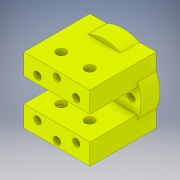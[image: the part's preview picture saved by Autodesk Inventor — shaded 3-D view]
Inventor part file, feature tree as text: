
AUTODESK INVENTOR PART (.ipt)
format: ipt  version: 2019 (Build 230136000, 136)  size: 233,472 bytes
history: native  units: mm
features: extrude x4, sketch x4, hole x1
ambient origin geometry x8: Origin, YZ Plane, XZ Plane, XY Plane, X Axis, Y Axis, Z Axis, Center Point
bodies: Solid1 (feature_tree)
feature tree (9):
  extrude  "Extrusion1"  Depth=10.5mm
  extrude  "Extrusion2"  Depth=80.0mm TaperAngle=360.0deg
  extrude  "Extrusion3"  Depth=10.0mm
  hole  "Hole1"  [1 undecoded]
  extrude  "Extrusion4"  Depth=10.0mm TaperAngle=0.0deg
  sketch  "Sketch1"  dims[d0=39.0mm d1=10.5mm]
  sketch  "Sketch2"  dims[d2=2.0mm d3=80.0mm d5=360.0deg]
  sketch  "Sketch4"  dims[d7=10.0mm d8=0.0mm d9=35.0mm]
  sketch  "Sketch5"  dims[d10=35.0mm d11=10.0mm d12=0.0mm d15=25.0mm d16=0.0mm d17=10.5mm d18=80.0mm d20=360.0deg d22=2.3mm d23=6.0mm d24=3.9mm d25=2.0mm d26=90.0deg d27=10.0mm d28=0.0mm d29=5.0mm d30=5.0mm d32=15.0mm d34=15.0mm d35=0.0mm d36=12.7mm d37=15.2mm d38=2.0mm d39=14.5mm d40=80.0mm d42=360.0deg d44=14.5mm d45=80.0mm d47=360.0deg]
note: 1 required parameter value undecoded (feature->parameter linkage not recoverable at this tier; creation-order binding heuristic only, values carry confidence <= 0.55)
